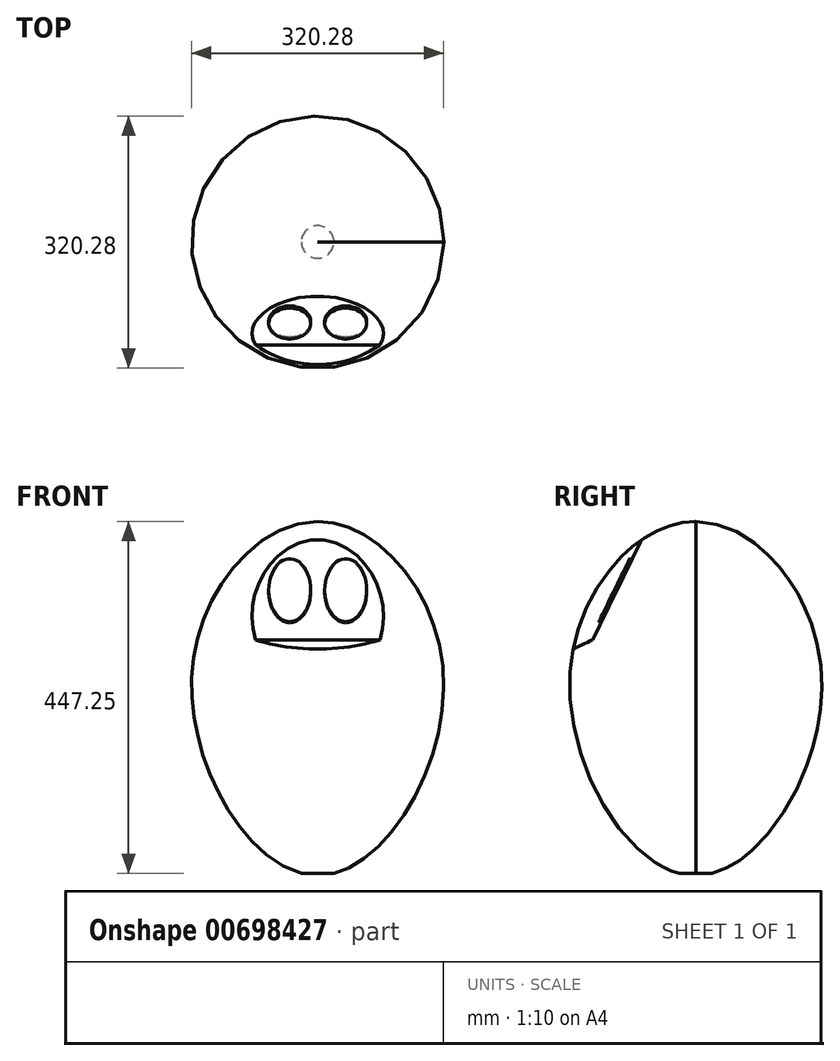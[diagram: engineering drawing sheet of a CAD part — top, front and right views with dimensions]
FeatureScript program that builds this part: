
annotation { "Feature Type Name" : "Feature", "Feature Type Description" : "" }
export const myFeature = defineFeature(function(context is Context, id is Id, definition is map)
    precondition{}
    {
        {
            var Q0;
            Q0=qCreatedBy(makeId("Front.planeOp"),FACE);
            var sketch = newSketch(context, id + "F0", { "sketchPlane" : qUnion([Q0])});
            skLineSegment(sketch, "E0", {"start": v(0, 0) * mm, "end": v(-160, 0) * mm, "construction": true});
            skLineSegment(sketch, "E1", {"start": v(0, 0) * mm, "end": v(0, -250) * mm});
            skLineSegment(sketch, "E2", {"start": v(0, 0) * mm, "end": v(160, 0) * mm, "construction": true});
            skLineSegment(sketch, "E3", {"start": v(0, 0) * mm, "end": v(0, 200) * mm});
            skFitSpline(sketch, "E4", {"points": [v(0, 200) * mm, v(-160, 0) * mm, v(0, -250) * mm, v(160, 0) * mm, v(0, 200) * mm]});
            skLineSegment(sketch, "E5", {"start": v(-20.64, -247.25) * mm, "end": v(20.64, -247.25) * mm});
            skSolve(sketch);
        }
        {
            var Q0;
            {var subQ0=sQuery(id+"F0.wireOp",EDGE,"E3");Q0=makeQuery(id+"F0.imprint","IMPRINT",FACE,{"disambiguationData":[TD([[makeQuery(id+"F0.imprint","IMPRINT",EDGE,{"derivedFrom":subQ0}),-1.0]])]});}
            var Q1;
            Q1=sQuery(id+"F0.wireOp",EDGE,"E3");
            revolve(context, id + "F1", {"entities" : qUnion([Q0]), "axis" : qUnion([Q1]), "revolveType" : RevolveType.FULL});
        }
        {
            var Q0;
            Q0=qCreatedBy(makeId("Right.planeOp"),FACE);
            var sketch = newSketch(context, id + "F2", { "sketchPlane" : qUnion([Q0])});
            skLineSegment(sketch, "E6", {"start": v(-254.04, -8.5) * mm, "end": v(-130.93, 49.83) * mm});
            skLineSegment(sketch, "E7", {"start": v(-130.93, 49.83) * mm, "end": v(-57.3, 200.37) * mm});
            skLineSegment(sketch, "E8", {"start": v(-57.3, 200.37) * mm, "end": v(-254.04, -8.5) * mm});
            skSolve(sketch);
        }
        {
            var Q0;
            Q0=makeQuery(id+"F2.imprint","IMPRINT",FACE,{"disambiguationData":[TD([[makeQuery(id+"F2.imprint","IMPRINT",EDGE,{"derivedFrom":sQuery(id+"F2.wireOp",EDGE,"E6")}),1.0]])]});
            extrude(context, id + "F3", {"entities" : qUnion([Q0]), "operationType" : NewBodyOperationType.REMOVE, "endBound" : BoundingType.SYMMETRIC, "depth" : 300 * mm, "offsetDistance" : 25 * mm});
        }
        {
            var Q0;
            Q0=makeQuery(id+"F3.boolean.opBoolean","COPY",FACE,{"derivedFrom":makeQuery(id+"F3.opExtrude","SWEPT_FACE",FACE,{"disambiguationData":[OSD([sQuery(id+"F2.wireOp",EDGE,"E7")])]})});
            var sketch = newSketch(context, id + "F4", { "sketchPlane" : qUnion([Q0])});
            skEllipse(sketch, "E9", {"center": v(-35.59, 55.9) * mm, "majorRadius": 44.64 * mm, "minorRadius": 26.7 * mm, "majorAxis": v(0, -1)});
            skEllipse(sketch, "E10.MirrorC", {"center": v(35.59, 55.9) * mm, "majorRadius": 44.64 * mm, "minorRadius": 26.7 * mm, "majorAxis": v(0, -1)});
            skSolve(sketch);
        }
        {
            var Q0;
            Q0=makeQuery(id+"F4.imprint","IMPRINT",FACE,{"disambiguationData":[TD([[makeQuery(id+"F4.imprint","IMPRINT",EDGE,{"derivedFrom":sQuery(id+"F4.wireOp",EDGE,"E9")}),1.0]])]});
            var Q1;
            Q1=makeQuery(id+"F4.imprint","IMPRINT",FACE,{"disambiguationData":[TD([[makeQuery(id+"F4.imprint","IMPRINT",EDGE,{"derivedFrom":sQuery(id+"F4.wireOp",EDGE,"E10.MirrorC")}),1.0]])]});
            extrude(context, id + "F5", {"entities" : qUnion([Q0, Q1]), "operationType" : NewBodyOperationType.ADD, "depth" : 3 * mm, "offsetDistance" : 25 * mm});
        }
    });
